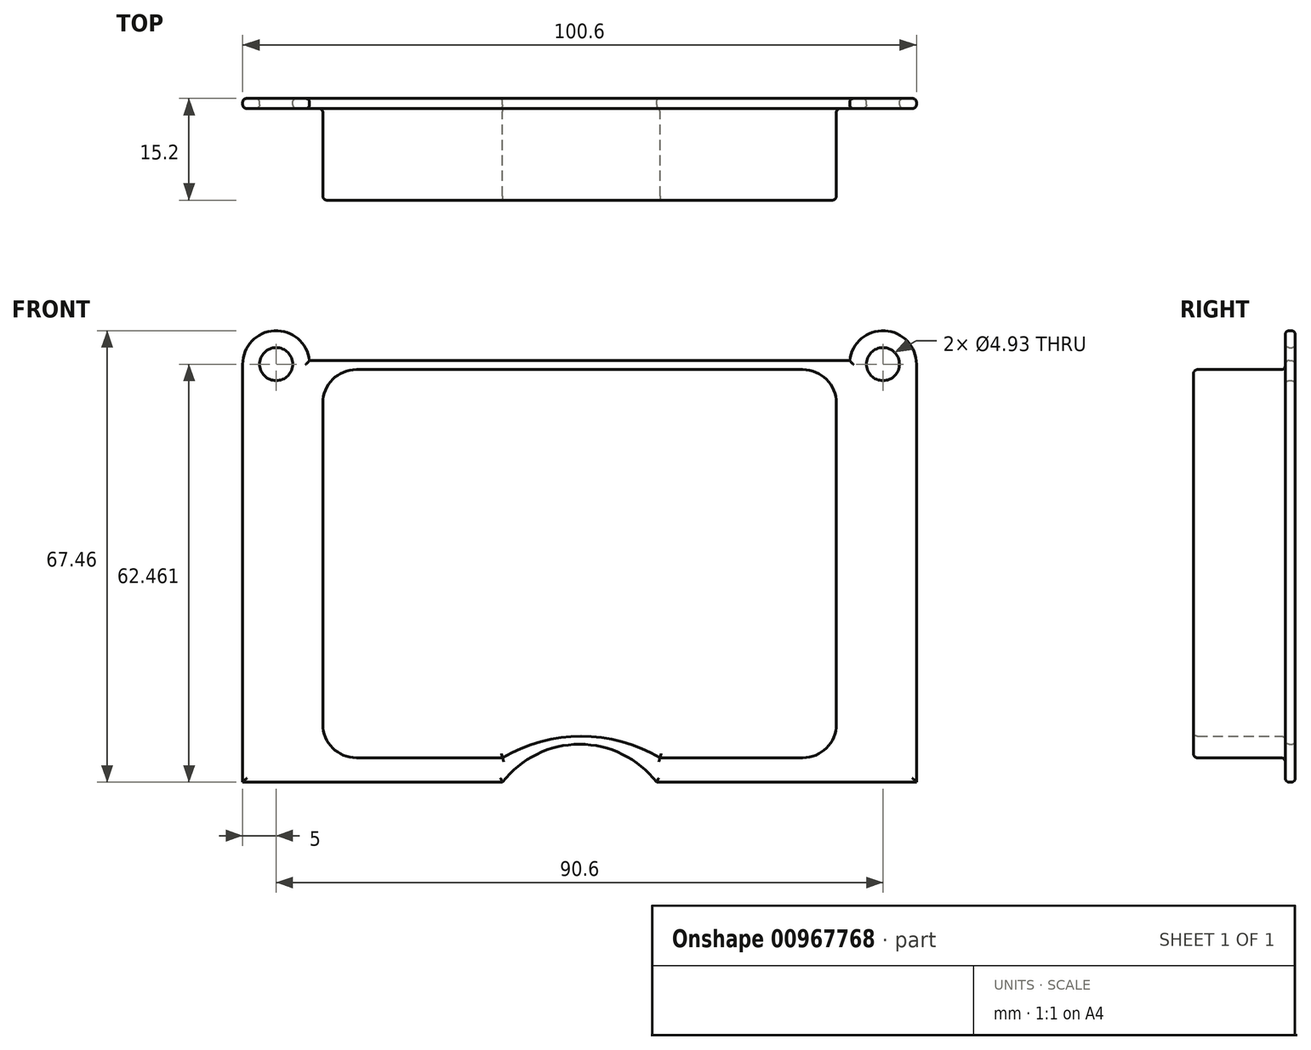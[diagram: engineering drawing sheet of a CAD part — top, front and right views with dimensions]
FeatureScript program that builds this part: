
annotation { "Feature Type Name" : "Feature", "Feature Type Description" : "" }
export const myFeature = defineFeature(function(context is Context, id is Id, definition is map)
    precondition{}
    {
        {
            var Q0;
            Q0=qCreatedBy(makeId("Front.planeOp"),FACE);
            var sketch = newSketch(context, id + "F0", { "sketchPlane" : qUnion([Q0])});
            skLineSegment(sketch, "E0.top", {"start": v(50.3, -32.64) * mm, "end": v(11.5, -32.64) * mm});
            skLineSegment(sketch, "E0.left", {"start": v(50.3, 29.82) * mm, "end": v(50.3, -32.64) * mm});
            skLineSegment(sketch, "E0.right", {"start": v(-50.3, 29.82) * mm, "end": v(-50.3, -32.64) * mm});
            skPoint(sketch, "E0.middle", {"position": v(0, 0) * mm});
            skLineSegment(sketch, "E1.bottom", {"start": v(33.33, 29) * mm, "end": v(-33.33, 29) * mm});
            skLineSegment(sketch, "E1.top", {"start": v(33.33, -29) * mm, "end": v(12, -29) * mm});
            skLineSegment(sketch, "E1.left", {"start": v(38.33, 24) * mm, "end": v(38.33, -24) * mm});
            skLineSegment(sketch, "E1.right", {"start": v(-38.33, 24) * mm, "end": v(-38.33, -24) * mm});
            skCircle(sketch, "E2", {"center": v(-45.3, 29.82) * mm, "radius": 2.46 * mm});
            skCircle(sketch, "E3", {"center": v(45.3, 29.82) * mm, "radius": 2.46 * mm});
            skArc(sketch, "E4", {"start": v(11.5, -32.64) * mm, "mid": v(0, -26.98) * mm, "end": v(-11.5, -32.64) * mm});
            skPoint(sketch, "E5.orphan", {"position": v(-38.33, 29) * mm});
            skPoint(sketch, "E6.orphan", {"position": v(38.33, 29) * mm});
            skPoint(sketch, "E7.orphan", {"position": v(38.33, -29) * mm});
            skLineSegment(sketch, "E8.trimOffspring", {"start": v(-11.5, -32.64) * mm, "end": v(-50.3, -32.64) * mm});
            skPoint(sketch, "E9.orphan", {"position": v(-38.33, -29) * mm});
            skArc(sketch, "E10", {"start": v(-40.33, 30.36) * mm, "mid": v(-45.57, 34.81) * mm, "end": v(-50.3, 29.82) * mm});
            skPoint(sketch, "E11.trimOffspring.end.orphan", {"position": v(-50.3, 32.64) * mm});
            skPoint(sketch, "E12.center.orphan", {"position": v(0, -29) * mm});
            skLineSegment(sketch, "E13.trimOffspring", {"start": v(-11.5, -29) * mm, "end": v(-33.33, -29) * mm});
            skArc(sketch, "E14", {"start": v(50.3, 29.82) * mm, "mid": v(45.57, 34.81) * mm, "end": v(40.33, 30.36) * mm});
            skPoint(sketch, "E15.orphan", {"position": v(50.3, 32.64) * mm});
            skLineSegment(sketch, "E16.trimOffspring", {"start": v(40.33, 30.36) * mm, "end": v(-40.33, 30.36) * mm});
            skArc(sketch, "E17", {"start": v(12, -29) * mm, "mid": v(0.25, -25.77) * mm, "end": v(-11.5, -29) * mm});
            skLineSegment(sketch, "E18", {"start": v(-33.33, 29) * mm, "end": v(-33.33, 29) * mm});
            skLineSegment(sketch, "E19", {"start": v(-38.33, 24) * mm, "end": v(-38.33, 24) * mm});
            skArc(sketch, "E20.filletArc", {"start": v(-33.33, 29) * mm, "mid": v(-36.87, 27.54) * mm, "end": v(-38.33, 24) * mm});
            skLineSegment(sketch, "E21", {"start": v(-38.33, -24) * mm, "end": v(-38.33, -24) * mm});
            skLineSegment(sketch, "E22", {"start": v(-33.33, -29) * mm, "end": v(-33.33, -29) * mm});
            skLineSegment(sketch, "E23", {"start": v(38.33, -24) * mm, "end": v(38.33, -24) * mm});
            skLineSegment(sketch, "E24", {"start": v(33.33, -29) * mm, "end": v(33.33, -29) * mm});
            skArc(sketch, "E25.filletArc", {"start": v(-38.33, -24) * mm, "mid": v(-36.87, -27.54) * mm, "end": v(-33.33, -29) * mm});
            skArc(sketch, "E26.filletArc", {"start": v(33.33, -29) * mm, "mid": v(36.87, -27.54) * mm, "end": v(38.33, -24) * mm});
            skLineSegment(sketch, "E27", {"start": v(33.33, 29) * mm, "end": v(33.33, 29) * mm});
            skLineSegment(sketch, "E28", {"start": v(38.33, 24) * mm, "end": v(38.33, 24) * mm});
            skArc(sketch, "E29.filletArc", {"start": v(38.33, 24) * mm, "mid": v(36.87, 27.54) * mm, "end": v(33.33, 29) * mm});
            skSolve(sketch);
        }
        {
            var Q0;
            Q0=makeQuery(id+"F0.imprint","IMPRINT",FACE,{"disambiguationData":[TD([[makeQuery(id+"F0.imprint","IMPRINT",EDGE,{"derivedFrom":sQuery(id+"F0.wireOp",EDGE,"E0.top")}),-1.0]])]});
            extrude(context, id + "F1", {"entities" : qUnion([Q0]), "depth" : 1.5 * mm, "offsetDistance" : 25 * mm});
        }
        {
            var Q0;
            Q0=makeQuery(id+"F0.imprint","IMPRINT",FACE,{"disambiguationData":[TD([[makeQuery(id+"F0.imprint","IMPRINT",EDGE,{"derivedFrom":sQuery(id+"F0.wireOp",EDGE,"E1.bottom")}),1.0]])]});
            extrude(context, id + "F2", {"entities" : qUnion([Q0]), "operationType" : NewBodyOperationType.ADD, "depth" : 15.2 * mm, "offsetDistance" : 25 * mm});
        }
        {
            var Q0;
            Q0=makeQuery(id+"F2.opExtrude","CAP_FACE",FACE,{"disambiguationData":[OSD([sQuery(id+"F0.wireOp",EDGE,"E1.bottom"),sQuery(id+"F0.wireOp",EDGE,"E1.top"),sQuery(id+"F0.wireOp",EDGE,"E1.left"),sQuery(id+"F0.wireOp",EDGE,"E1.right"),sQuery(id+"F0.wireOp",EDGE,"t8jTAduY-borm-6WBk-gXmm-hGUWCT9EdZjI"),sQuery(id+"F0.wireOp",EDGE,"nTkVIfJ2-Npkp-3oju-LrXJ-VCYWRT61dK0M"),sQuery(id+"F0.wireOp",EDGE,"ZcDn8Pa6-COEi-NUnx-naSF-wVXIizopYO8T"),sQuery(id+"F0.wireOp",EDGE,"cFVNjpfB-YAlo-Z2SV-Uzdh-rk5Ovnh4bPEo"),sQuery(id+"F0.wireOp",EDGE,"E13.trimOffspring"),sQuery(id+"F0.wireOp",EDGE,"E17")])],"isStart":false});
            var Q1;
            Q1=makeQuery(id+"F1.opExtrude","CAP_FACE",FACE,{"disambiguationData":[OSD([sQuery(id+"F0.wireOp",EDGE,"E0.top"),sQuery(id+"F0.wireOp",EDGE,"E0.left"),sQuery(id+"F0.wireOp",EDGE,"E0.right"),sQuery(id+"F0.wireOp",EDGE,"E1.bottom"),sQuery(id+"F0.wireOp",EDGE,"E1.top"),sQuery(id+"F0.wireOp",EDGE,"E1.left"),sQuery(id+"F0.wireOp",EDGE,"E1.right"),sQuery(id+"F0.wireOp",EDGE,"E2"),sQuery(id+"F0.wireOp",EDGE,"E3"),sQuery(id+"F0.wireOp",EDGE,"E4"),sQuery(id+"F0.wireOp",EDGE,"t8jTAduY-borm-6WBk-gXmm-hGUWCT9EdZjI"),sQuery(id+"F0.wireOp",EDGE,"nTkVIfJ2-Npkp-3oju-LrXJ-VCYWRT61dK0M"),sQuery(id+"F0.wireOp",EDGE,"E8.trimOffspring"),sQuery(id+"F0.wireOp",EDGE,"ZcDn8Pa6-COEi-NUnx-naSF-wVXIizopYO8T"),sQuery(id+"F0.wireOp",EDGE,"E10"),sQuery(id+"F0.wireOp",EDGE,"cFVNjpfB-YAlo-Z2SV-Uzdh-rk5Ovnh4bPEo"),sQuery(id+"F0.wireOp",EDGE,"E13.trimOffspring"),sQuery(id+"F0.wireOp",EDGE,"E14"),sQuery(id+"F0.wireOp",EDGE,"E16.trimOffspring"),sQuery(id+"F0.wireOp",EDGE,"E17")])],"isStart":false});
            var Q2;
            {var subQ0=sQuery(id+"F0.wireOp",EDGE,"E17");var subQ1=sQuery(id+"F0.wireOp",EDGE,"E13.trimOffspring");var subQ2=sQuery(id+"F0.wireOp",EDGE,"cFVNjpfB-YAlo-Z2SV-Uzdh-rk5Ovnh4bPEo");var subQ3=sQuery(id+"F0.wireOp",EDGE,"ZcDn8Pa6-COEi-NUnx-naSF-wVXIizopYO8T");var subQ4=sQuery(id+"F0.wireOp",EDGE,"nTkVIfJ2-Npkp-3oju-LrXJ-VCYWRT61dK0M");var subQ5=sQuery(id+"F0.wireOp",EDGE,"t8jTAduY-borm-6WBk-gXmm-hGUWCT9EdZjI");var subQ6=sQuery(id+"F0.wireOp",EDGE,"E1.right");var subQ7=sQuery(id+"F0.wireOp",EDGE,"E1.left");var subQ8=sQuery(id+"F0.wireOp",EDGE,"E1.top");var subQ9=sQuery(id+"F0.wireOp",EDGE,"E1.bottom");Q2=makeQuery(id+"F2.boolean.opBoolean","MERGE",FACE,{"derivedFrom":[makeQuery(id+"F1.opExtrude","CAP_FACE",FACE,{"disambiguationData":[OSD([sQuery(id+"F0.wireOp",EDGE,"E0.top"),sQuery(id+"F0.wireOp",EDGE,"E0.left"),sQuery(id+"F0.wireOp",EDGE,"E0.right"),subQ9,subQ8,subQ7,subQ6,sQuery(id+"F0.wireOp",EDGE,"E2"),sQuery(id+"F0.wireOp",EDGE,"E3"),sQuery(id+"F0.wireOp",EDGE,"E4"),subQ5,subQ4,sQuery(id+"F0.wireOp",EDGE,"E8.trimOffspring"),subQ3,sQuery(id+"F0.wireOp",EDGE,"E10"),subQ2,subQ1,sQuery(id+"F0.wireOp",EDGE,"E14"),sQuery(id+"F0.wireOp",EDGE,"E16.trimOffspring"),subQ0])],"isStart":true}),makeQuery(id+"F2.opExtrude","CAP_FACE",FACE,{"disambiguationData":[OSD([subQ9,subQ8,subQ7,subQ6,subQ5,subQ4,subQ3,subQ2,subQ1,subQ0])],"isStart":true})]});}
            fillet(context, id + "F3", {"entities" : qUnion([Q0, Q1, Q2]), "radius" : 0.6 * mm, "tangentPropagation" : true, "allowEdgeOverflow" : false});
        }
    });
